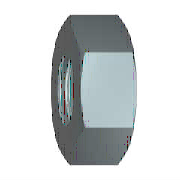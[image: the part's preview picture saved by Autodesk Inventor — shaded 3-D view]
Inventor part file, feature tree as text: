
AUTODESK INVENTOR PART (.ipt)
format: ipt  version: 2021 (Build 250183000, 183)  size: 173,568 bytes
history: native  units: mm (DEFAULTED — no unit token found)
features: sketch x3, chamfer x1, hole x1, other x1, plane x1
ambient origin geometry x7: Origin, YZ Plane, XZ Plane, X Axis, Y Axis, Z Axis, Center Point
bodies: Solid1 (feature_tree), Body (feature_tree)
feature tree (7):
  chamfer  "Chamfer1"  Angle=30.0deg  [1 undecoded]
  hole  "Thread"  [1 undecoded]
  other  "Work Axis1"
  plane  "Work Plane1"
  sketch  "Sketch1"  dims[d0=8.082904mm]
  sketch  "Sketch2"  dims[d1=3.2mm]
  sketch  "Sketch3"  dims[d2=0.0mm d3=30.0deg d4=30.0deg d5=7.0mm d6=7.0mm d7=90.0deg d25=3.242mm d26=6.0mm d27=4.0mm d28=2.0mm d29=14.3117mm d30=8.0mm d31=20.594885mm d8=0.378886mm d9=30.0deg d10=0.378886mm d11=30.0deg d13=0.0mm d14=0.0mm d39=0.0mm d40=0.378886mm d41=0.378886mm d42=0.0mm]
note: 2 required parameter values undecoded (feature->parameter linkage not recoverable at this tier; creation-order binding heuristic only, values carry confidence <= 0.55)
